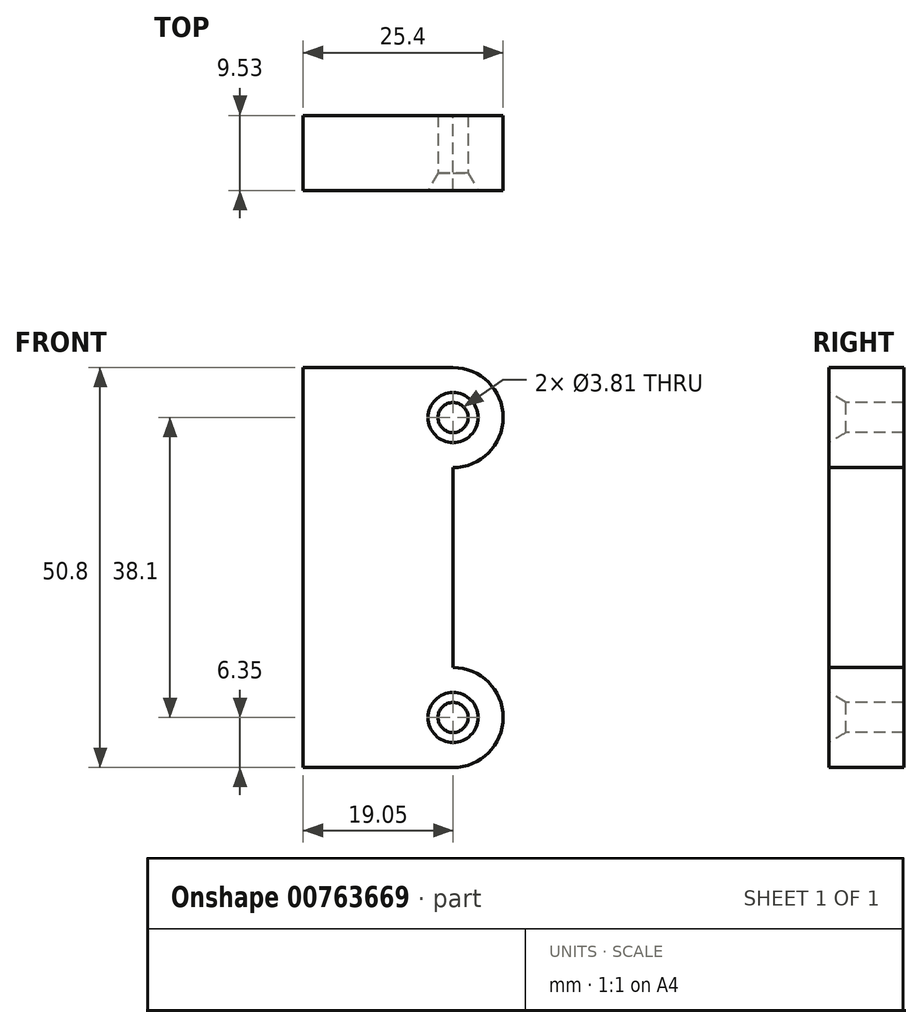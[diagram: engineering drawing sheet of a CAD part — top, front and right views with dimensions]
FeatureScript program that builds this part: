
annotation { "Feature Type Name" : "Feature", "Feature Type Description" : "" }
export const myFeature = defineFeature(function(context is Context, id is Id, definition is map)
    precondition{}
    {
        {
            var Q0;
            Q0=qCreatedBy(makeId("Front.planeOp"),FACE);
            var sketch = newSketch(context, id + "F0", { "sketchPlane" : qUnion([Q0])});
            skLineSegment(sketch, "E0.bottom", {"start": v(0, 0) * mm, "end": v(12.7, 0) * mm, "construction": true});
            skLineSegment(sketch, "E0.top", {"start": v(0, 50.8) * mm, "end": v(12.7, 50.8) * mm, "construction": true});
            skLineSegment(sketch, "E0.left", {"start": v(0, 0) * mm, "end": v(0, 50.8) * mm, "construction": true});
            skLineSegment(sketch, "E0.right", {"start": v(12.7, 0) * mm, "end": v(12.7, 50.8) * mm, "construction": true});
            skLineSegment(sketch, "E1", {"start": v(0, 0) * mm, "end": v(0, 50.8) * mm});
            skLineSegment(sketch, "E2", {"start": v(0, 50.8) * mm, "end": v(19.05, 50.8) * mm});
            skLineSegment(sketch, "E3", {"start": v(19.05, 0) * mm, "end": v(0, 0) * mm});
            skArc(sketch, "E4", {"start": v(19.05, 38.1) * mm, "mid": v(25.4, 44.45) * mm, "end": v(19.05, 50.8) * mm});
            skArc(sketch, "E5", {"start": v(19.05, 0) * mm, "mid": v(25.4, 6.35) * mm, "end": v(19.05, 12.7) * mm});
            skLineSegment(sketch, "E6", {"start": v(19.05, 12.7) * mm, "end": v(19.05, 38.1) * mm});
            skSolve(sketch);
        }
        {
            var Q0;
            Q0 = qSketchRegion(id + "F0", true);
            extrude(context, id + "F1", {"entities" : qUnion([Q0]), "depth" : 9.52 * mm, "offsetDistance" : 25.4 * mm});
        }
        {
            var Q0;
            Q0=makeQuery(id+"F1.opExtrude","CAP_FACE",FACE,{"disambiguationData":[OSD([sQuery(id+"F0.wireOp",EDGE,"E1"),sQuery(id+"F0.wireOp",EDGE,"E2"),sQuery(id+"F0.wireOp",EDGE,"E3"),sQuery(id+"F0.wireOp",EDGE,"E4"),sQuery(id+"F0.wireOp",EDGE,"E5"),sQuery(id+"F0.wireOp",EDGE,"E6")])],"isStart":false});
            var sketch = newSketch(context, id + "F2", { "sketchPlane" : qUnion([Q0])});
            skPoint(sketch, "E7", {"position": v(19.05, 44.45) * mm});
            skPoint(sketch, "E8", {"position": v(19.05, 6.35) * mm});
            skSolve(sketch);
        }
        {
            var Q0;
            Q0=sQuery(id+"F2.wireOp",VERTEX,"E7");
            var Q1;
            Q1=sQuery(id+"F2.wireOp",VERTEX,"E8");
            var Q2;
            Q2=makeQuery(id+"F1.opExtrude","SWEPT_BODY",BODY,{"disambiguationData":[OSD([sQuery(id+"F0.wireOp",EDGE,"E1"),sQuery(id+"F0.wireOp",EDGE,"E2"),sQuery(id+"F0.wireOp",EDGE,"E3"),sQuery(id+"F0.wireOp",EDGE,"E4"),sQuery(id+"F0.wireOp",EDGE,"E5"),sQuery(id+"F0.wireOp",EDGE,"E6")])]});
            hole(context, id + "F3", {"style" : HoleStyle.C_SINK, "endStyle" : HoleEndStyle.THROUGH, "holeDiameter" : 3.8 * mm, "cSinkDiameter" : 6.35 * mm, "cSinkAngle" : 60 * degree, "majorDiameter" : 6.35 * mm, "isTappedThrough" : true, "tappedDepth" : 12.7 * mm, "tapClearance" : 3, "startFromSketch" : true, "locations" : qUnion([Q0, Q1]), "scope" : qUnion([Q2])});
        }
    });
